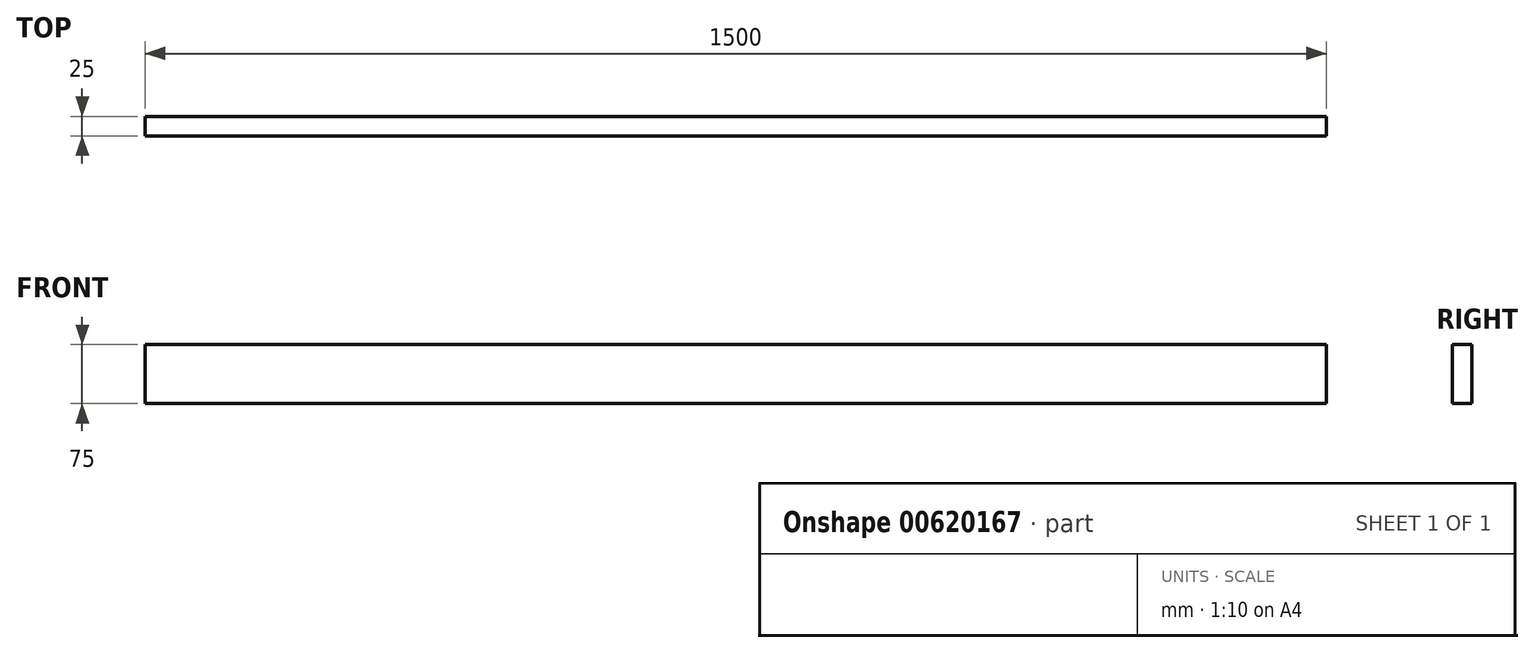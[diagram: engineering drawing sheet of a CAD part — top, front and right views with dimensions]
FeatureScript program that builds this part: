
annotation { "Feature Type Name" : "Feature", "Feature Type Description" : "" }
export const myFeature = defineFeature(function(context is Context, id is Id, definition is map)
    precondition{}
    {
        {
            var Q0;
            Q0=qCreatedBy(makeId("Front.planeOp"),FACE);
            var sketch = newSketch(context, id + "F0", { "sketchPlane" : qUnion([Q0])});
            skLineSegment(sketch, "E0.bottom", {"start": v(750, 37.5) * mm, "end": v(-750, 37.5) * mm});
            skLineSegment(sketch, "E0.top", {"start": v(750, -37.5) * mm, "end": v(-750, -37.5) * mm});
            skLineSegment(sketch, "E0.left", {"start": v(750, 37.5) * mm, "end": v(750, -37.5) * mm});
            skLineSegment(sketch, "E0.right", {"start": v(-750, 37.5) * mm, "end": v(-750, -37.5) * mm});
            skPoint(sketch, "E0.middle", {"position": v(0, 0) * mm});
            skSolve(sketch);
        }
        {
            var Q0;
            Q0=makeQuery(id+"F0.imprint","IMPRINT",FACE,{"disambiguationData":[TD([[makeQuery(id+"F0.imprint","IMPRINT",EDGE,{"derivedFrom":sQuery(id+"F0.wireOp",EDGE,"E0.bottom")}),1.0]])]});
            extrude(context, id + "F1", {"entities" : qUnion([Q0]), "depth" : 25 * mm, "offsetDistance" : 25 * mm});
        }
    });
